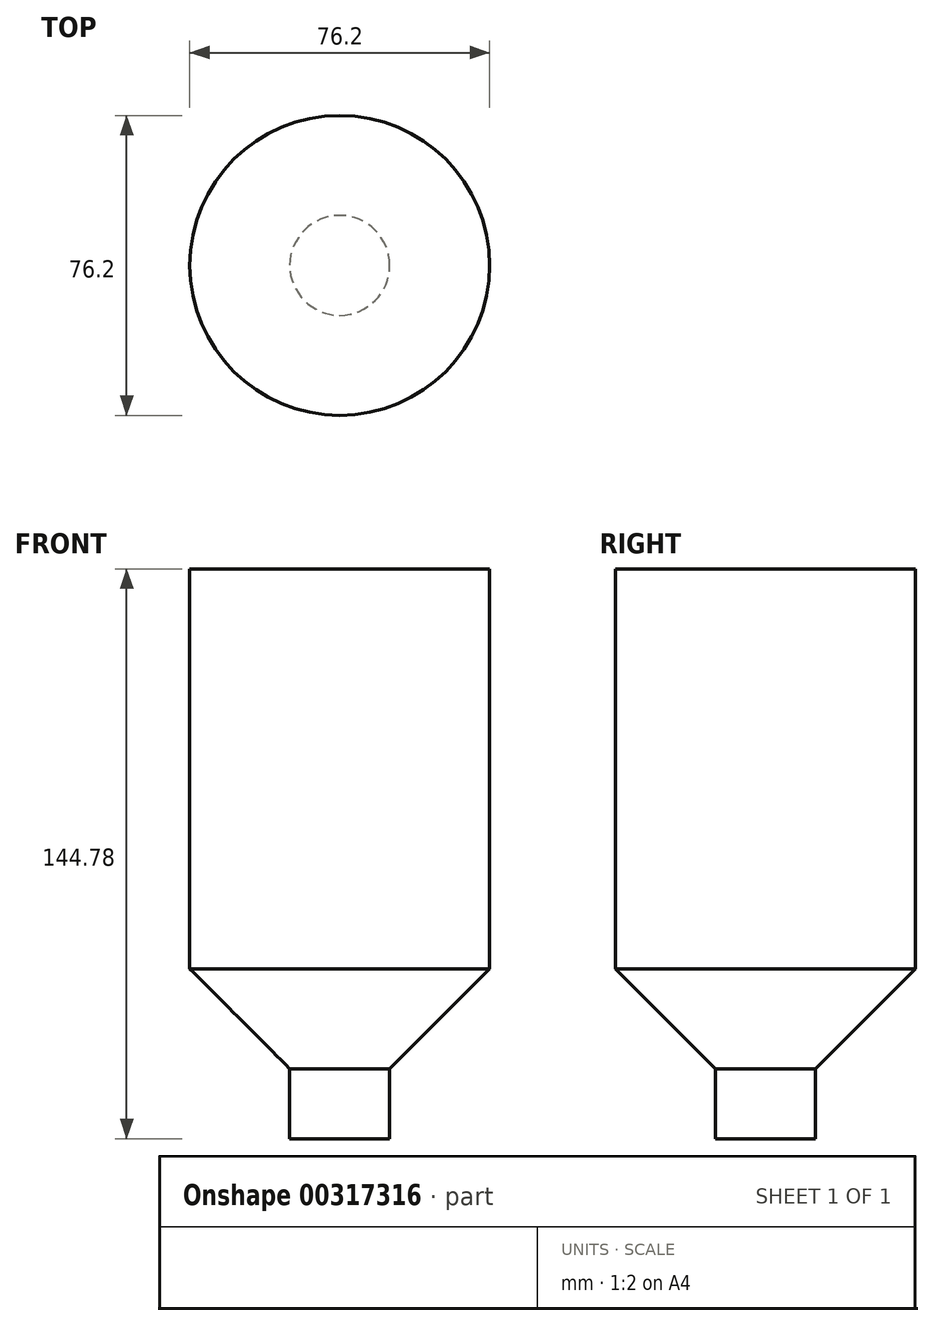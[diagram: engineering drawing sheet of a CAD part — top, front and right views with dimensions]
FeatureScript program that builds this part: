
annotation { "Feature Type Name" : "Feature", "Feature Type Description" : "" }
export const myFeature = defineFeature(function(context is Context, id is Id, definition is map)
    precondition{}
    {
        {
            var Q0;
            Q0=qCreatedBy(makeId("Top.planeOp"),FACE);
            var sketch = newSketch(context, id + "F0", { "sketchPlane" : qUnion([Q0])});
            skCircle(sketch, "E0", {"center": v(0, 0) * mm, "radius": 38.1 * mm});
            skSolve(sketch);
        }
        {
            var Q0;
            Q0 = qSketchRegion(id + "F0", true);
            extrude(context, id + "F1", {"entities" : qUnion([Q0]), "oppositeDirection" : true, "depth" : 101.6 * mm});
        }
        {
            var Q0;
            Q0=makeQuery(id+"F1.opExtrude","CAP_FACE",FACE,{"disambiguationData":[OSD([sQuery(id+"F0.wireOp",EDGE,"E0")])],"isStart":false});
            var sketch = newSketch(context, id + "F2", { "sketchPlane" : qUnion([Q0])});
            skCircle(sketch, "E1", {"center": v(0, 0) * mm, "radius": 38.1 * mm});
            skSolve(sketch);
        }
        {
            var Q0;
            Q0 = qSketchRegion(id + "F2", true);
            extrude(context, id + "F3", {"entities" : qUnion([Q0]), "operationType" : NewBodyOperationType.ADD, "depth" : 25.4 * mm, "hasDraft" : true, "draftAngle" : 45 * degree, "draftPullDirection" : true});
        }
        {
            var Q0;
            Q0=makeQuery(id+"F3.opExtrude","CAP_FACE",FACE,{"disambiguationData":[OSD([sQuery(id+"F2.wireOp",EDGE,"E1")])],"isStart":false});
            var sketch = newSketch(context, id + "F4", { "sketchPlane" : qUnion([Q0])});
            skCircle(sketch, "E2", {"center": v(0, 0) * mm, "radius": 12.7 * mm});
            skSolve(sketch);
        }
        {
            var Q0;
            Q0 = qSketchRegion(id + "F4", true);
            extrude(context, id + "F5", {"entities" : qUnion([Q0]), "operationType" : NewBodyOperationType.ADD, "depth" : 17.78 * mm});
        }
    });
